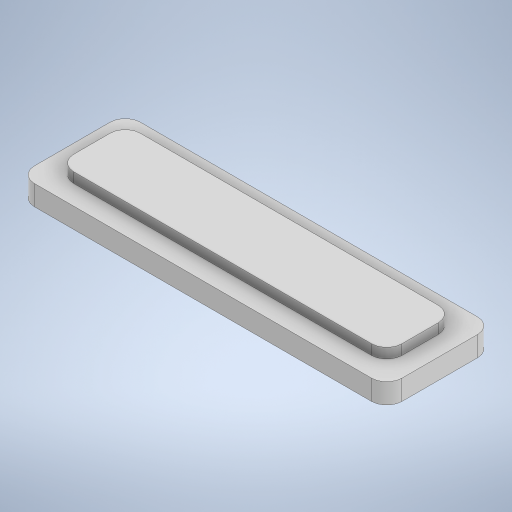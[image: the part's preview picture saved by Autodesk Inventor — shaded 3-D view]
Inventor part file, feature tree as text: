
AUTODESK INVENTOR PART (.ipt)
format: ipt  version: 2024 (Build 280153000, 153)  size: 256,512 bytes
history: native  units: mm
features: extrude x2, sketch x1
ambient origin geometry x8: Origin, YZ Plane, XZ Plane, XY Plane, X Axis, Y Axis, Z Axis, Center Point
bodies: Body1 (feature_tree)
feature tree (3):
  sketch  "Эскиз1"
  extrude  "Выдавливание3"  Depth=1.5mm
  extrude  "Выдавливание4"  Depth=1.5mm
